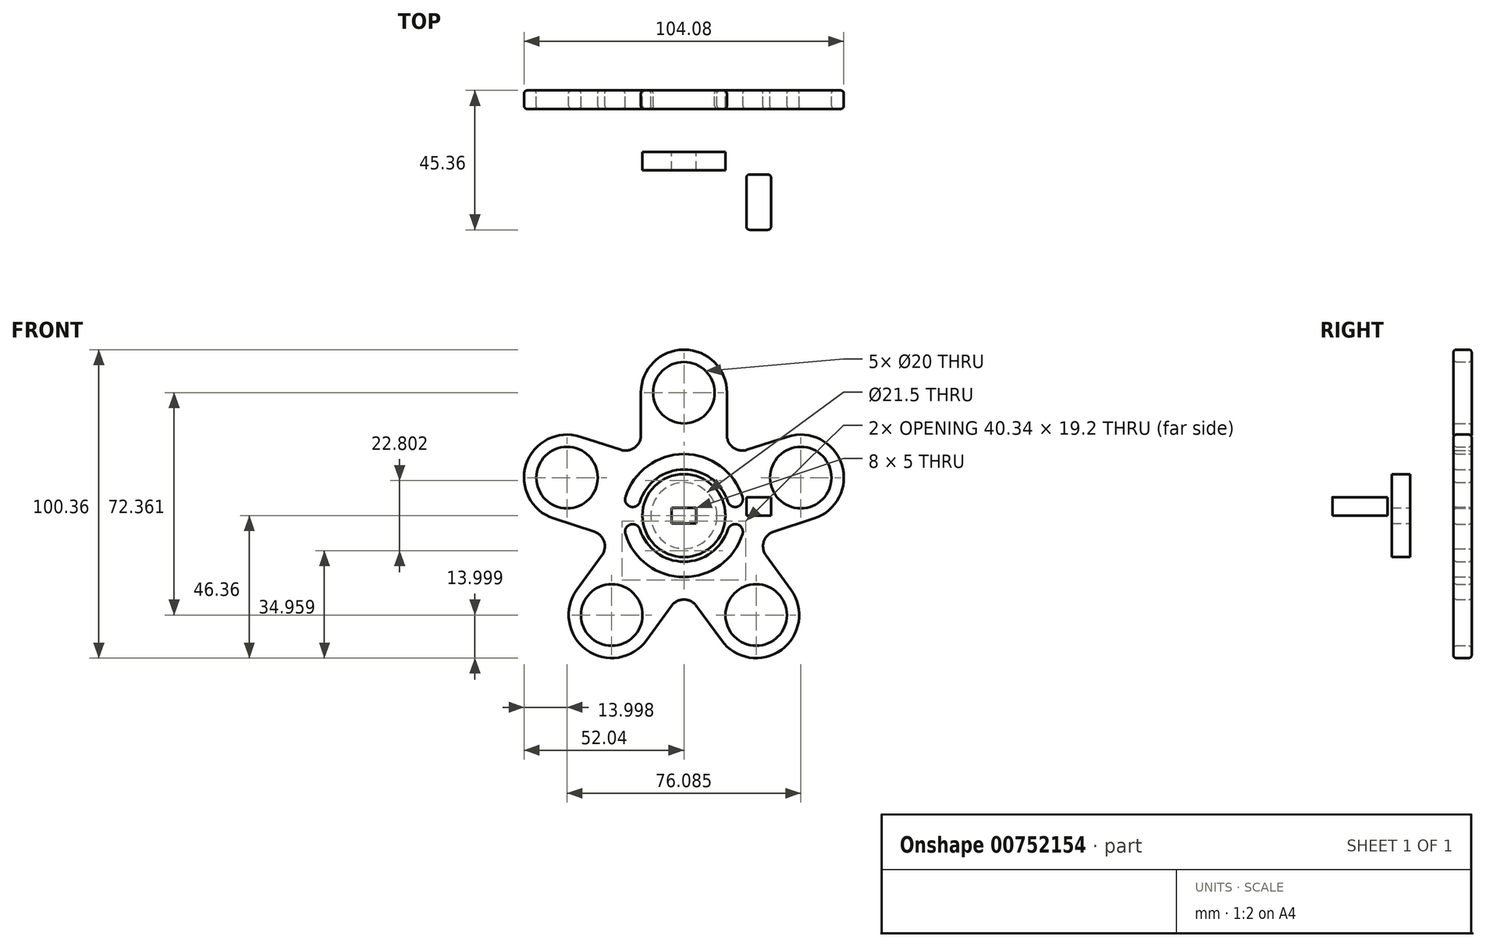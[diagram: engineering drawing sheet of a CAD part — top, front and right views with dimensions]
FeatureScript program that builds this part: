
annotation { "Feature Type Name" : "Feature", "Feature Type Description" : "" }
export const myFeature = defineFeature(function(context is Context, id is Id, definition is map)
    precondition{}
    {
        {
            var Q0;
            Q0=qCreatedBy(makeId("Front.planeOp"),FACE);
            var sketch = newSketch(context, id + "F0", { "sketchPlane" : qUnion([Q0])});
            skCircle(sketch, "E0", {"center": v(0, 0) * mm, "radius": 10.75 * mm});
            skLineSegment(sketch, "E1", {"start": v(0, 0) * mm, "end": v(0, 40) * mm, "construction": true});
            skCircle(sketch, "E2", {"center": v(0, 40) * mm, "radius": 10 * mm});
            skCircle(sketch, "E3.1.0", {"center": v(-38.04, 12.36) * mm, "radius": 10 * mm});
            skCircle(sketch, "E3.2.0", {"center": v(-23.51, -32.36) * mm, "radius": 10 * mm});
            skCircle(sketch, "E3.3.0", {"center": v(23.51, -32.36) * mm, "radius": 10 * mm});
            skCircle(sketch, "E3.4.0", {"center": v(38.04, 12.36) * mm, "radius": 10 * mm});
            skLineSegment(sketch, "E4.left", {"start": v(14, 40) * mm, "end": v(14, 26.15) * mm});
            skLineSegment(sketch, "E4.right", {"start": v(-14, 40) * mm, "end": v(-14, 26.15) * mm});
            skArc(sketch, "E5", {"start": v(14, 40) * mm, "mid": v(0, 54) * mm, "end": v(-14, 40) * mm});
            skLineSegment(sketch, "E6.1.0", {"start": v(-33.72, 25.68) * mm, "end": v(-20.55, 21.4) * mm});
            skArc(sketch, "E6.1.1", {"start": v(-33.72, 25.68) * mm, "mid": v(-51.36, 16.69) * mm, "end": v(-42.37, -0.95) * mm});
            skLineSegment(sketch, "E6.1.2", {"start": v(-42.37, -0.95) * mm, "end": v(-29.2, -5.23) * mm});
            skLineSegment(sketch, "E6.2.0", {"start": v(-34.84, -24.13) * mm, "end": v(-26.7, -12.93) * mm});
            skArc(sketch, "E6.2.1", {"start": v(-34.84, -24.13) * mm, "mid": v(-31.74, -43.69) * mm, "end": v(-12.19, -40.59) * mm});
            skLineSegment(sketch, "E6.2.2", {"start": v(-12.19, -40.59) * mm, "end": v(-4.05, -29.39) * mm});
            skLineSegment(sketch, "E6.3.0", {"start": v(12.19, -40.59) * mm, "end": v(4.05, -29.39) * mm});
            skArc(sketch, "E6.3.1", {"start": v(12.19, -40.59) * mm, "mid": v(31.74, -43.69) * mm, "end": v(34.84, -24.13) * mm});
            skLineSegment(sketch, "E6.3.2", {"start": v(34.84, -24.13) * mm, "end": v(26.7, -12.93) * mm});
            skLineSegment(sketch, "E6.4.0", {"start": v(42.37, -0.95) * mm, "end": v(29.2, -5.23) * mm});
            skArc(sketch, "E6.4.1", {"start": v(42.37, -0.95) * mm, "mid": v(51.36, 16.69) * mm, "end": v(33.72, 25.68) * mm});
            skLineSegment(sketch, "E6.4.2", {"start": v(33.72, 25.68) * mm, "end": v(20.55, 21.4) * mm});
            skPoint(sketch, "E7.orphan", {"position": v(-17.5, -0.27) * mm});
            skPoint(sketch, "E8.orphan", {"position": v(-14.31, -10.07) * mm});
            skPoint(sketch, "E9.orphan", {"position": v(-5.15, -16.72) * mm});
            skPoint(sketch, "E10.orphan", {"position": v(5.15, -16.72) * mm});
            skPoint(sketch, "E11.orphan", {"position": v(14.31, -10.07) * mm});
            skPoint(sketch, "E12.orphan", {"position": v(17.5, -0.27) * mm});
            skArc(sketch, "E13.filletArc", {"start": v(-20.55, 21.4) * mm, "mid": v(-16.06, 22.1) * mm, "end": v(-14, 26.15) * mm});
            skArc(sketch, "E14.filletArc", {"start": v(14, 26.15) * mm, "mid": v(16.06, 22.1) * mm, "end": v(20.55, 21.4) * mm});
            skPoint(sketch, "E15.visualSharp", {"position": v(22.65, -7.36) * mm});
            skArc(sketch, "E15.filletArc", {"start": v(29.2, -5.23) * mm, "mid": v(25.99, -8.44) * mm, "end": v(26.7, -12.93) * mm});
            skPoint(sketch, "E16.visualSharp", {"position": v(0, -23.82) * mm});
            skArc(sketch, "E16.filletArc", {"start": v(4.05, -29.39) * mm, "mid": v(0, -27.32) * mm, "end": v(-4.05, -29.39) * mm});
            skPoint(sketch, "E17.visualSharp", {"position": v(-22.65, -7.36) * mm});
            skArc(sketch, "E17.filletArc", {"start": v(-26.7, -12.93) * mm, "mid": v(-25.99, -8.44) * mm, "end": v(-29.2, -5.23) * mm});
            skArc(sketch, "E18", {"start": v(-16.68, -5.29) * mm, "mid": v(0, -17.5) * mm, "end": v(16.68, -5.29) * mm});
            skArc(sketch, "E19.trimOffspring", {"start": v(16.68, 5.29) * mm, "mid": v(0, 17.5) * mm, "end": v(-16.68, 5.29) * mm});
            skArc(sketch, "E20.0.startCap", {"start": v(19.06, 6.05) * mm, "mid": v(17.44, 2.9) * mm, "end": v(14.3, 4.53) * mm});
            skArc(sketch, "E20.0.endCap", {"start": v(-14.3, 4.53) * mm, "mid": v(-17.44, 2.9) * mm, "end": v(-19.06, 6.05) * mm});
            skArc(sketch, "E20.0.left", {"start": v(14.3, 4.53) * mm, "mid": v(0, 15) * mm, "end": v(-14.3, 4.53) * mm});
            skArc(sketch, "E20.0.right", {"start": v(19.06, 6.05) * mm, "mid": v(0, 20) * mm, "end": v(-19.06, 6.05) * mm});
            skArc(sketch, "E21.0.startCap", {"start": v(-19.06, -6.05) * mm, "mid": v(-17.44, -2.9) * mm, "end": v(-14.3, -4.53) * mm});
            skArc(sketch, "E21.0.endCap", {"start": v(14.3, -4.53) * mm, "mid": v(17.44, -2.9) * mm, "end": v(19.06, -6.05) * mm});
            skArc(sketch, "E21.0.left", {"start": v(-14.3, -4.53) * mm, "mid": v(0, -15) * mm, "end": v(14.3, -4.53) * mm});
            skArc(sketch, "E21.0.right", {"start": v(-19.06, -6.05) * mm, "mid": v(0, -20) * mm, "end": v(19.06, -6.05) * mm});
            skSolve(sketch);
        }
        {
            var Q0;
            Q0=makeQuery(id+"F0.imprint","IMPRINT",FACE,{"disambiguationData":[TD([[makeQuery(id+"F0.imprint","IMPRINT",EDGE,{"derivedFrom":sQuery(id+"F0.wireOp",EDGE,"E0")}),-1.0]])]});
            extrude(context, id + "F1", {"entities" : qUnion([Q0]), "depth" : 6 * mm, "offsetDistance" : 25 * mm});
        }
        {
            var Q0;
            Q0=makeQuery(id+"F1.opExtrude","CAP_FACE",FACE,{"disambiguationData":[OSD([sQuery(id+"F0.wireOp",EDGE,"E0"),sQuery(id+"F0.wireOp",EDGE,"E2"),sQuery(id+"F0.wireOp",EDGE,"E3.1.0"),sQuery(id+"F0.wireOp",EDGE,"E3.2.0"),sQuery(id+"F0.wireOp",EDGE,"E3.3.0"),sQuery(id+"F0.wireOp",EDGE,"E3.4.0"),sQuery(id+"F0.wireOp",EDGE,"E4.left"),sQuery(id+"F0.wireOp",EDGE,"E4.right"),sQuery(id+"F0.wireOp",EDGE,"E5"),sQuery(id+"F0.wireOp",EDGE,"E6.1.0"),sQuery(id+"F0.wireOp",EDGE,"E6.1.1"),sQuery(id+"F0.wireOp",EDGE,"E6.1.2"),sQuery(id+"F0.wireOp",EDGE,"E6.2.0"),sQuery(id+"F0.wireOp",EDGE,"E6.2.1"),sQuery(id+"F0.wireOp",EDGE,"E6.2.2"),sQuery(id+"F0.wireOp",EDGE,"E6.3.0"),sQuery(id+"F0.wireOp",EDGE,"E6.3.1"),sQuery(id+"F0.wireOp",EDGE,"E6.3.2"),sQuery(id+"F0.wireOp",EDGE,"E6.4.0"),sQuery(id+"F0.wireOp",EDGE,"E6.4.1"),sQuery(id+"F0.wireOp",EDGE,"E6.4.2"),sQuery(id+"F0.wireOp",EDGE,"E13.filletArc"),sQuery(id+"F0.wireOp",EDGE,"E14.filletArc"),sQuery(id+"F0.wireOp",EDGE,"E15.filletArc"),sQuery(id+"F0.wireOp",EDGE,"E16.filletArc"),sQuery(id+"F0.wireOp",EDGE,"E17.filletArc")])],"isStart":false});
            var Q1;
            Q1=makeQuery(id+"F1.opExtrude","CAP_FACE",FACE,{"disambiguationData":[OSD([sQuery(id+"F0.wireOp",EDGE,"E0"),sQuery(id+"F0.wireOp",EDGE,"E2"),sQuery(id+"F0.wireOp",EDGE,"E3.1.0"),sQuery(id+"F0.wireOp",EDGE,"E3.2.0"),sQuery(id+"F0.wireOp",EDGE,"E3.3.0"),sQuery(id+"F0.wireOp",EDGE,"E3.4.0"),sQuery(id+"F0.wireOp",EDGE,"E4.left"),sQuery(id+"F0.wireOp",EDGE,"E4.right"),sQuery(id+"F0.wireOp",EDGE,"E5"),sQuery(id+"F0.wireOp",EDGE,"E6.1.0"),sQuery(id+"F0.wireOp",EDGE,"E6.1.1"),sQuery(id+"F0.wireOp",EDGE,"E6.1.2"),sQuery(id+"F0.wireOp",EDGE,"E6.2.0"),sQuery(id+"F0.wireOp",EDGE,"E6.2.1"),sQuery(id+"F0.wireOp",EDGE,"E6.2.2"),sQuery(id+"F0.wireOp",EDGE,"E6.3.0"),sQuery(id+"F0.wireOp",EDGE,"E6.3.1"),sQuery(id+"F0.wireOp",EDGE,"E6.3.2"),sQuery(id+"F0.wireOp",EDGE,"E6.4.0"),sQuery(id+"F0.wireOp",EDGE,"E6.4.1"),sQuery(id+"F0.wireOp",EDGE,"E6.4.2"),sQuery(id+"F0.wireOp",EDGE,"E13.filletArc"),sQuery(id+"F0.wireOp",EDGE,"E14.filletArc"),sQuery(id+"F0.wireOp",EDGE,"E15.filletArc"),sQuery(id+"F0.wireOp",EDGE,"E16.filletArc"),sQuery(id+"F0.wireOp",EDGE,"E17.filletArc")])],"isStart":true});
            fillet(context, id + "F2", {"entities" : qUnion([Q0, Q1]), "radius" : 1 * mm, "tangentPropagation" : true, "allowEdgeOverflow" : false});
        }
        {
            var Q0;
            Q0=qCreatedBy(makeId("Top.planeOp"),FACE);
            var sketch = newSketch(context, id + "F3", { "sketchPlane" : qUnion([Q0])});
            skLineSegment(sketch, "E22.bottom", {"start": v(21.35, -27.36) * mm, "end": v(27.35, -27.36) * mm});
            skLineSegment(sketch, "E22.top", {"start": v(21.35, -45.36) * mm, "end": v(27.35, -45.36) * mm});
            skLineSegment(sketch, "E22.left", {"start": v(20.35, -28.36) * mm, "end": v(20.35, -44.36) * mm});
            skLineSegment(sketch, "E22.right", {"start": v(28.35, -28.36) * mm, "end": v(28.35, -44.36) * mm});
            skPoint(sketch, "E22.middle", {"position": v(24.35, -36.36) * mm});
            skPoint(sketch, "E23.visualSharp", {"position": v(20.35, -45.36) * mm});
            skArc(sketch, "E23.filletArc", {"start": v(20.35, -44.36) * mm, "mid": v(20.64, -45.06) * mm, "end": v(21.35, -45.36) * mm});
            skPoint(sketch, "E24.visualSharp", {"position": v(28.35, -45.36) * mm});
            skArc(sketch, "E24.filletArc", {"start": v(27.35, -45.36) * mm, "mid": v(28.05, -45.06) * mm, "end": v(28.35, -44.36) * mm});
            skPoint(sketch, "E25.visualSharp", {"position": v(28.35, -27.36) * mm});
            skArc(sketch, "E25.filletArc", {"start": v(28.35, -28.36) * mm, "mid": v(28.05, -27.65) * mm, "end": v(27.35, -27.36) * mm});
            skPoint(sketch, "E26.visualSharp", {"position": v(20.35, -27.36) * mm});
            skArc(sketch, "E26.filletArc", {"start": v(21.35, -27.36) * mm, "mid": v(20.64, -27.65) * mm, "end": v(20.35, -28.36) * mm});
            skSolve(sketch);
        }
        {
            var Q0;
            Q0=makeQuery(id+"F3.imprint","IMPRINT",FACE,{"disambiguationData":[TD([[makeQuery(id+"F3.imprint","IMPRINT",EDGE,{"derivedFrom":sQuery(id+"F3.wireOp",EDGE,"E22.bottom")}),-1.0]])]});
            extrude(context, id + "F4", {"entities" : qUnion([Q0]), "depth" : 6 * mm, "offsetDistance" : 25 * mm});
        }
        {
            var Q0;
            Q0=qCreatedBy(makeId("Front.planeOp"),FACE);
            var sketch = newSketch(context, id + "F5", { "sketchPlane" : qUnion([Q0])});
            skCircle(sketch, "E27", {"center": v(0, 0) * mm, "radius": 13.5 * mm});
            skLineSegment(sketch, "E28.bottom", {"start": v(4, -2.5) * mm, "end": v(-4, -2.5) * mm});
            skLineSegment(sketch, "E28.top", {"start": v(4, 2.5) * mm, "end": v(-4, 2.5) * mm});
            skLineSegment(sketch, "E28.left", {"start": v(4, -2.5) * mm, "end": v(4, 2.5) * mm});
            skLineSegment(sketch, "E28.right", {"start": v(-4, -2.5) * mm, "end": v(-4, 2.5) * mm});
            skSolve(sketch);
        }
        {
            var Q0;
            Q0 = qSketchRegion(id + "F5", true);
            extrude(context, id + "F6", {"entities" : qUnion([Q0]), "depth" : 26 * mm, "offsetDistance" : 25 * mm, "hasSecondDirection" : true, "secondDirectionOppositeDirection" : false, "secondDirectionDepth" : 20 * mm});
        }
    });
